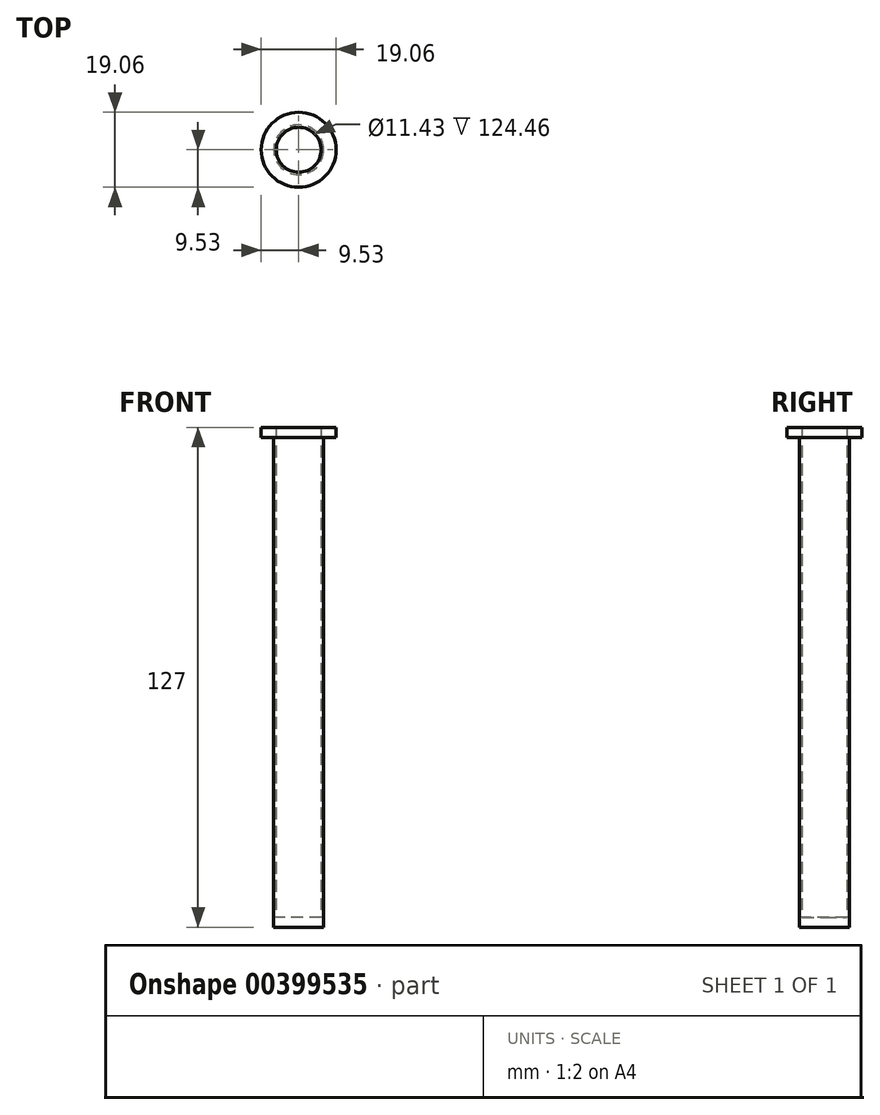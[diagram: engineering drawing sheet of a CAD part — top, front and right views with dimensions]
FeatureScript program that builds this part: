
annotation { "Feature Type Name" : "Feature", "Feature Type Description" : "" }
export const myFeature = defineFeature(function(context is Context, id is Id, definition is map)
    precondition{}
    {
        {
            var Q0;
            Q0=qCreatedBy(makeId("Top.planeOp"),FACE);
            var sketch = newSketch(context, id + "F0", { "sketchPlane" : qUnion([Q0])});
            skCircle(sketch, "E0", {"center": v(0, 0) * mm, "radius": 6.35 * mm});
            skCircle(sketch, "E1", {"center": v(0, 0) * mm, "radius": 5.72 * mm});
            skSolve(sketch);
        }
        {
            var Q0;
            Q0=makeQuery(id+"F0.imprint","IMPRINT",FACE,{"disambiguationData":[TD([[makeQuery(id+"F0.imprint","IMPRINT",EDGE,{"derivedFrom":sQuery(id+"F0.wireOp",EDGE,"E0")}),1.0]])]});
            extrude(context, id + "F1", {"entities" : qUnion([Q0]), "depth" : 127 * mm});
        }
        {
            var Q0;
            Q0=makeQuery(id+"F1.opExtrude","CAP_FACE",FACE,{"disambiguationData":[OSD([sQuery(id+"F0.wireOp",EDGE,"E0"),sQuery(id+"F0.wireOp",EDGE,"E1")])],"isStart":true});
            var sketch = newSketch(context, id + "F2", { "sketchPlane" : qUnion([Q0])});
            skCircle(sketch, "E2", {"center": v(0, 0) * mm, "radius": 5.8 * mm});
            skSolve(sketch);
        }
        {
            var Q0;
            Q0=makeQuery(id+"F2.imprint","IMPRINT",FACE,{"disambiguationData":[TD([[makeQuery(id+"F2.imprint","IMPRINT",EDGE,{"derivedFrom":makeQuery(id+"F1.opExtrude","CAP_EDGE",EDGE,{"disambiguationData":[OSD([sQuery(id+"F0.wireOp",EDGE,"E1")])],"isStart":true})}),-1.0]])]});
            extrude(context, id + "F3", {"entities" : qUnion([Q0]), "operationType" : NewBodyOperationType.ADD, "depth" : -2.54 * mm});
        }
        {
            var Q0;
            Q0=makeQuery(id+"F1.opExtrude","CAP_FACE",FACE,{"disambiguationData":[OSD([sQuery(id+"F0.wireOp",EDGE,"E0"),sQuery(id+"F0.wireOp",EDGE,"E1")])],"isStart":false});
            var sketch = newSketch(context, id + "F4", { "sketchPlane" : qUnion([Q0])});
            skCircle(sketch, "E3", {"center": v(0, 0) * mm, "radius": 9.53 * mm});
            skSolve(sketch);
        }
        {
            var Q0;
            Q0=makeQuery(id+"F4.imprint","IMPRINT",FACE,{"disambiguationData":[TD([[makeQuery(id+"F4.imprint","IMPRINT",EDGE,{"derivedFrom":sQuery(id+"F4.wireOp",EDGE,"E3")}),1.0]])]});
            extrude(context, id + "F5", {"entities" : qUnion([Q0]), "operationType" : NewBodyOperationType.ADD, "depth" : -2.54 * mm});
        }
    });
